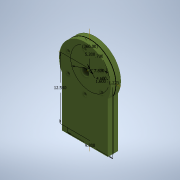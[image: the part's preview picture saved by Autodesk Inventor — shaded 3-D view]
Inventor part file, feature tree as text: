
AUTODESK INVENTOR PART (.ipt)
format: ipt  version: 2021.1 (Build 251245000, 245)  size: 138,752 bytes
history: native  units: in
note: dims shown in document units (in); Inventor stores cm internally (conversion verified against a paired STEP export)
features: sketch x2, extrude x2
ambient origin geometry x8: Origin, YZ Plane, XZ Plane, XY Plane, X Axis, Y Axis, Z Axis, Center Point
bodies: Solid1 (feature_tree)
feature tree (4):
  sketch  "Sketch1"  dims[d0=10.4in d1=7.8in]
  extrude  "Extrusion1"  Depth=7.8in
  sketch  "Sketch2"  dims[d8=0.7in d9=2.3622in d11=360.0deg d13=1.6in d14=1.0in d15=0.0in d16=5.2in d17=9.2in d18=4.6in d19=12.5in d20=1.2225in d21=2.0in d22=0.0in]
  extrude  "Extrusion2"  Depth=2.0in TaperAngle=360.0deg
